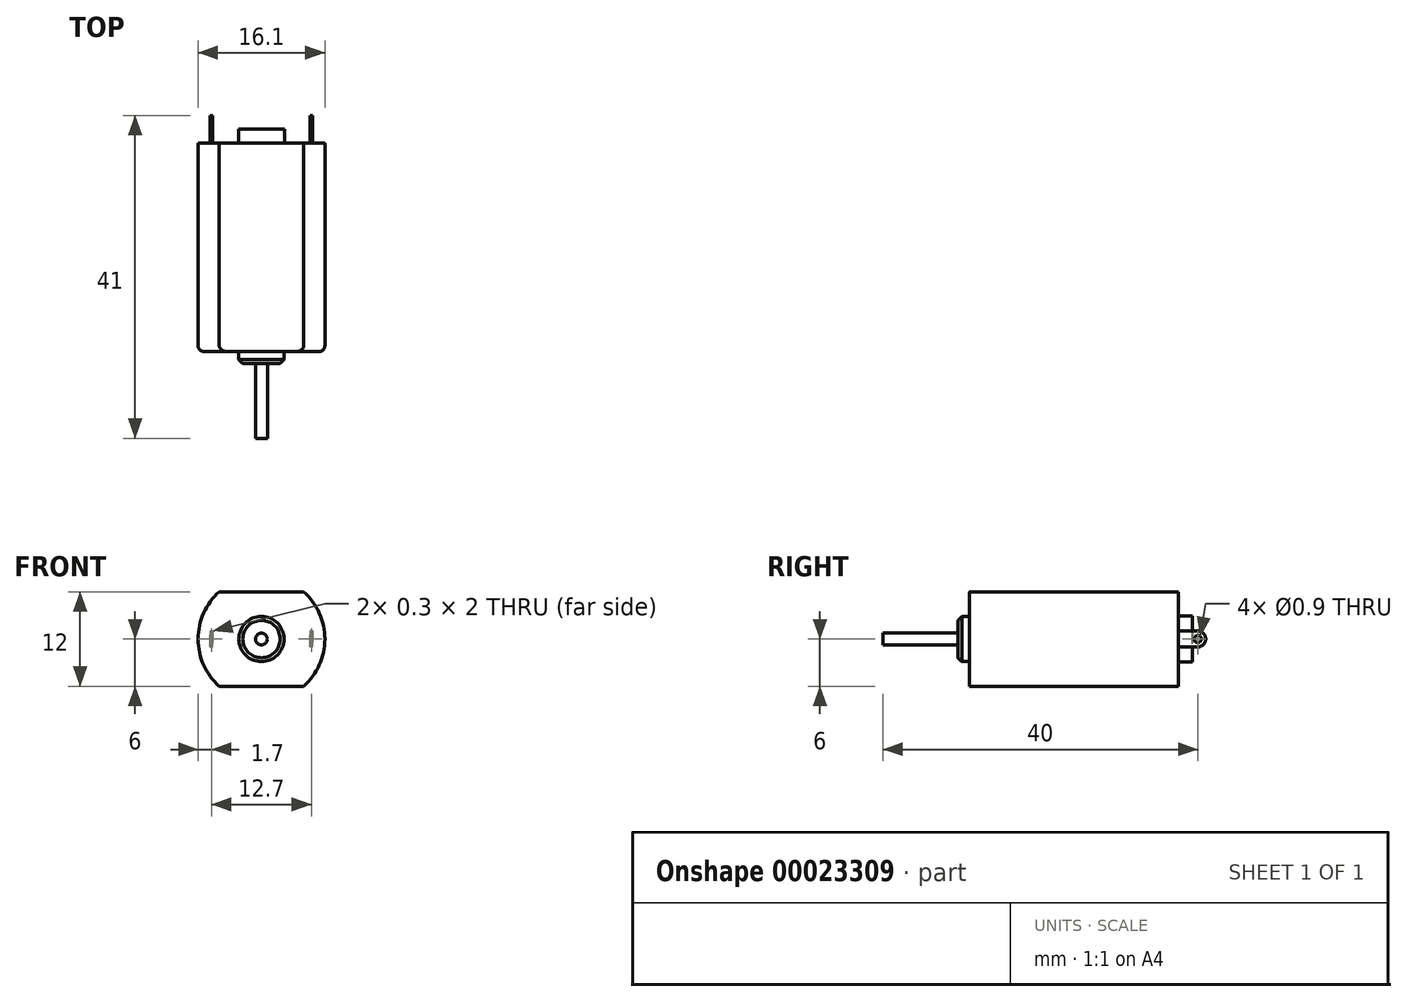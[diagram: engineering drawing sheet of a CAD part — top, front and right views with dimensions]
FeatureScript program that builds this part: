
annotation { "Feature Type Name" : "Feature", "Feature Type Description" : "" }
export const myFeature = defineFeature(function(context is Context, id is Id, definition is map)
    precondition{}
    {
        {
            var Q0;
            Q0=qCreatedBy(makeId("Front.planeOp"),FACE);
            var sketch = newSketch(context, id + "F0", { "sketchPlane" : qUnion([Q0])});
            skCircle(sketch, "E0", {"center": v(0, 0) * mm, "radius": 8.05 * mm});
            skSolve(sketch);
        }
        {
            var Q0;
            Q0 = qSketchRegion(id + "F0", true);
            var Q1;
            Q1=sQuery(id+"F0.wireOp",EDGE,"E0");
            extrude(context, id + "F1", {"entities" : qUnion([Q0]), "surfaceEntities" : qUnion([Q1]), "oppositeDirection" : true, "depth" : 26.5 * mm});
        }
        {
            var Q0;
            Q0=makeQuery(id+"F1.opExtrude","CAP_FACE",FACE,{"disambiguationData":[OSD([sQuery(id+"F0.wireOp",EDGE,"E0")])],"isStart":true});
            var sketch = newSketch(context, id + "F2", { "sketchPlane" : qUnion([Q0])});
            skLineSegment(sketch, "E1", {"start": v(-5.37, 6) * mm, "end": v(5.37, 6) * mm});
            skLineSegment(sketch, "E2", {"start": v(-5.37, -6) * mm, "end": v(5.37, -6) * mm});
            skArc(sketch, "E3", {"start": v(5.37, 6) * mm, "mid": v(0, 8.05) * mm, "end": v(-5.37, 6) * mm});
            skArc(sketch, "E4", {"start": v(-5.37, -6) * mm, "mid": v(0, -8.05) * mm, "end": v(5.37, -6) * mm});
            skSolve(sketch);
        }
        {
            var Q0;
            Q0 = qSketchRegion(id + "F2", true);
            extrude(context, id + "F3", {"entities" : qUnion([Q0]), "operationType" : NewBodyOperationType.REMOVE, "endBound" : BoundingType.UP_TO_NEXT, "oppositeDirection" : true, "depth" : 25 * mm});
        }
        {
            var Q0;
            Q0=qCreatedBy(makeId("Front.planeOp"),FACE);
            var sketch = newSketch(context, id + "F4", { "sketchPlane" : qUnion([Q0])});
            skCircle(sketch, "E5", {"center": v(0, 0) * mm, "radius": 2.87 * mm});
            skSolve(sketch);
        }
        {
            var Q0;
            Q0=makeQuery(id+"F1.opExtrude","CAP_FACE",FACE,{"disambiguationData":[OSD([sQuery(id+"F0.wireOp",EDGE,"E0")])],"isStart":true});
            var sketch = newSketch(context, id + "F5", { "sketchPlane" : qUnion([Q0])});
            skCircle(sketch, "E6", {"center": v(0, 0) * mm, "radius": 0.75 * mm});
            skSolve(sketch);
        }
        {
            var Q0;
            Q0 = qSketchRegion(id + "F5", true);
            extrude(context, id + "F6", {"entities" : qUnion([Q0]), "operationType" : NewBodyOperationType.ADD, "depth" : 11 * mm});
        }
        {
            var Q0;
            Q0 = qSketchRegion(id + "F4", true);
            extrude(context, id + "F7", {"entities" : qUnion([Q0]), "operationType" : NewBodyOperationType.ADD, "depth" : 1.5 * mm});
        }
        {
            var Q0;
            Q0 = qSketchRegion(id + "F4", true);
            extrude(context, id + "F8", {"entities" : qUnion([Q0]), "operationType" : NewBodyOperationType.ADD, "depth" : 1.5 * mm});
        }
        {
            var Q0;
            Q0=makeQuery(id+"F1.opExtrude","CAP_FACE",FACE,{"disambiguationData":[OSD([sQuery(id+"F0.wireOp",EDGE,"E0")])],"isStart":false});
            var sketch = newSketch(context, id + "F9", { "sketchPlane" : qUnion([Q0])});
            skCircle(sketch, "E7", {"center": v(0, 0) * mm, "radius": 2.93 * mm});
            skSolve(sketch);
        }
        {
            var Q0;
            Q0 = qSketchRegion(id + "F9", true);
            extrude(context, id + "F10", {"entities" : qUnion([Q0]), "operationType" : NewBodyOperationType.ADD, "depth" : 1.8 * mm});
        }
        {
            var Q0;
            Q0=qCreatedBy(makeId("Right.planeOp"),FACE);
            cPlane(context, id + "F11", {"entities" : qUnion([Q0]), "cplaneType" : CPlaneType.OFFSET, "offset" : 6.2 * mm, "width" : 150 * mm, "height" : 150 * mm});
        }
        {
            var Q0;
            Q0=qCreatedBy(id+"F11.planeOp",FACE);
            var sketch = newSketch(context, id + "F12", { "sketchPlane" : qUnion([Q0])});
            skLineSegment(sketch, "E8", {"start": v(29, 1) * mm, "end": v(26.5, 1) * mm});
            skLineSegment(sketch, "E9", {"start": v(26.5, 1) * mm, "end": v(26.5, -1) * mm});
            skLineSegment(sketch, "E10", {"start": v(26.5, -1) * mm, "end": v(29, -1) * mm});
            skArc(sketch, "E11", {"start": v(29, -1) * mm, "mid": v(30, 0) * mm, "end": v(29, 1) * mm});
            skCircle(sketch, "E12", {"center": v(29, 0) * mm, "radius": 0.45 * mm});
            skSolve(sketch);
        }
        {
            var Q0;
            Q0=makeQuery(id+"F12.imprint","IMPRINT",FACE,{"disambiguationData":[TD([[makeQuery(id+"F12.imprint","IMPRINT",EDGE,{"derivedFrom":sQuery(id+"F12.wireOp",EDGE,"E8")}),1.0]])]});
            extrude(context, id + "F13", {"entities" : qUnion([Q0]), "depth" : 0.3 * mm});
        }
        {
            var Q0;
            Q0=makeQuery(id+"F13.opExtrude","SWEPT_BODY",BODY,{"disambiguationData":[OSD([sQuery(id+"F12.wireOp",EDGE,"E8"),sQuery(id+"F12.wireOp",EDGE,"E9"),sQuery(id+"F12.wireOp",EDGE,"E10"),sQuery(id+"F12.wireOp",EDGE,"E11"),sQuery(id+"F12.wireOp",EDGE,"E12")])]});
            var Q1;
            Q1=qCreatedBy(makeId("Right.planeOp"),FACE);
            mirror(context, id + "F14", {"operationType" : NewBodyOperationType.ADD, "entities" : qUnion([Q0]), "mirrorPlane" : qUnion([Q1])});
        }
        {
            var Q0;
            Q0=makeQuery(id+"F3.boolean.opBoolean","COPY",EDGE,{"derivedFrom":makeQuery(id+"F3.opExtrude","CAP_EDGE",EDGE,{"disambiguationData":[OSD([sQuery(id+"F2.wireOp",EDGE,"E1")])],"isStart":true})});
            var Q1;
            Q1=makeQuery(id+"F3.boolean.opBoolean","SPLIT",EDGE,{"disambiguationData":[OD(1.0)],"derivedFrom":makeQuery(id+"F1.opExtrude","CAP_EDGE",EDGE,{"disambiguationData":[OSD([sQuery(id+"F0.wireOp",EDGE,"E0")])],"isStart":true})});
            var Q2;
            Q2=makeQuery(id+"F3.boolean.opBoolean","COPY",EDGE,{"derivedFrom":makeQuery(id+"F3.opExtrude","CAP_EDGE",EDGE,{"disambiguationData":[OSD([sQuery(id+"F2.wireOp",EDGE,"E2")])],"isStart":true})});
            var Q3;
            Q3=makeQuery(id+"F3.boolean.opBoolean","SPLIT",EDGE,{"disambiguationData":[OD(0.0)],"derivedFrom":makeQuery(id+"F1.opExtrude","CAP_EDGE",EDGE,{"disambiguationData":[OSD([sQuery(id+"F0.wireOp",EDGE,"E0")])],"isStart":true})});
            fillet(context, id + "F15", {"entities" : qUnion([Q0, Q1, Q2, Q3]), "radius" : 0.75 * mm, "tangentPropagation" : true, "allowEdgeOverflow" : false});
        }
        {
            var Q0;
            Q0=makeQuery(id+"F7.opExtrude","CAP_EDGE",EDGE,{"disambiguationData":[OSD([sQuery(id+"F4.wireOp",EDGE,"E5")])],"isStart":false});
            chamfer(context, id + "F16", {"entities" : qUnion([Q0]), "width" : 0.5 * mm, "tangentPropagation" : true});
        }
        {
            var Q0;
            Q0=makeQuery(id+"F1.opExtrude","SWEPT_BODY",BODY,{"disambiguationData":[OSD([sQuery(id+"F0.wireOp",EDGE,"E0")])]});
            transform(context, id + "F17", {"entities" : qUnion([Q0]), "transformType" : TransformType.TRANSLATION_3D, "dx" : 0 * mm, "dy" : 0 * mm, "dz" : 0 * mm, "makeCopy" : true});
        }
    });
